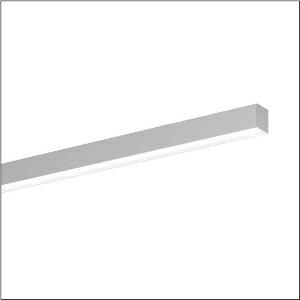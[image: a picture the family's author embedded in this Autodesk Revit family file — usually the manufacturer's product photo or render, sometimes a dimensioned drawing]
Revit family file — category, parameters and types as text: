
# Revit family: silica_r__21_51mx20da42sb_9e9a
name_source: partatom
category: Lighting Fixtures
units: mm (PartAtom-declared; Revit-internal decimal feet)

## family parameters
Cut with Voids When Loaded = No
Host = Face
Light Source = No
Part Type = Normal
Room Calculation Point = No
Round Connector Dimension = Use Diameter
Shared = No

## types (1)
- --- (1 x LED, 2400 lm, 15.2 W, 4000K)
    Apparent Load = 15 VA
    CIE Flux Codes = 48 79 96 100 100
    Color Rendering = 80
    Color Temperature = 4000K
    Default Elevation = 1800 mm
    Description = Silica® 21, office luminaire, primary optical cover: cover, of PMMA, opal, light emission: direct distribution, primary light characteristic: symmetric, installation type: surface-mounted, LED, rated luminous flux: 2.400lm, luminous efficacy: 158lm/W, light colour: 840, colour temperature: 4000K, with terminal, 3+2-pole, max. 2.5mm², mains connection: 220..240V, AC, 50/60Hz, rated input power: 15.2W, luminaire housing, of aluminium, metallic grey (RAL 9006), length: 1.204mm, width: 53mm, height: 53mm, protection rating (complete): IP20, insulation class (complete): insulation class I (protective earthing), certification: CE, permissible operating ambient temperature: 0..+35°C, standard: EN 50419, packaging unit: 1 piece
    Height = 0 mm  [stored 0 ft]
    Lamp = 1 x LED
    Lamp Light Flux = 2400 lm
    Lamp Power = 15.2 W
    Lamp count = 1
    Length = 1204 mm
    Luminous efficacy = 158 lm/W
    Manufacturer = Siteco
    ModVariant = No
    Model = 51MX20DA42SB
    Mounting Place = Ceiling
    Mounting Type = Recessed
    Number of Poles = 1
    OnlyDefault = Yes
    Power Factor = 1
    Product Name = Silica® 21
    Product group = office luminaire | ceiling recessed
    ProductGroupID = 400
    Protection Class = Protection class I
    Protection Degree = IP 20
    RLX_Detail_Level = 1
    RLX_Emergency_Light_Flux = 0 lm
    RLX_Emergency_Type = 0
    RLX_Emergency_Type_DB = No
    RlxData = <blob elided: 26265 chars, md5=d1b93d47>
    Socket = socket
    Standby Power = 0 W
    System Light Flux = 2400 lm
    System Power = 15 W
    Type Comments = factory setting: luminous flux: 100 % | dim-lin: 254 | 218 mA
    Type Image = l_1335933.jpg
    URL = http://relux.com
    VarID = @adj_087017
    Voltage = 0 V
    Weight = 0.00 kg
    Width = 53 mm

note: [stored X ft] marks values corroborated as IEEE doubles in the binary element streams (Revit-internal decimal feet)

## geometry (parser evidence)
native form markers: Blend x4, Sweep x9
no freeform markers — native parametric forms only
